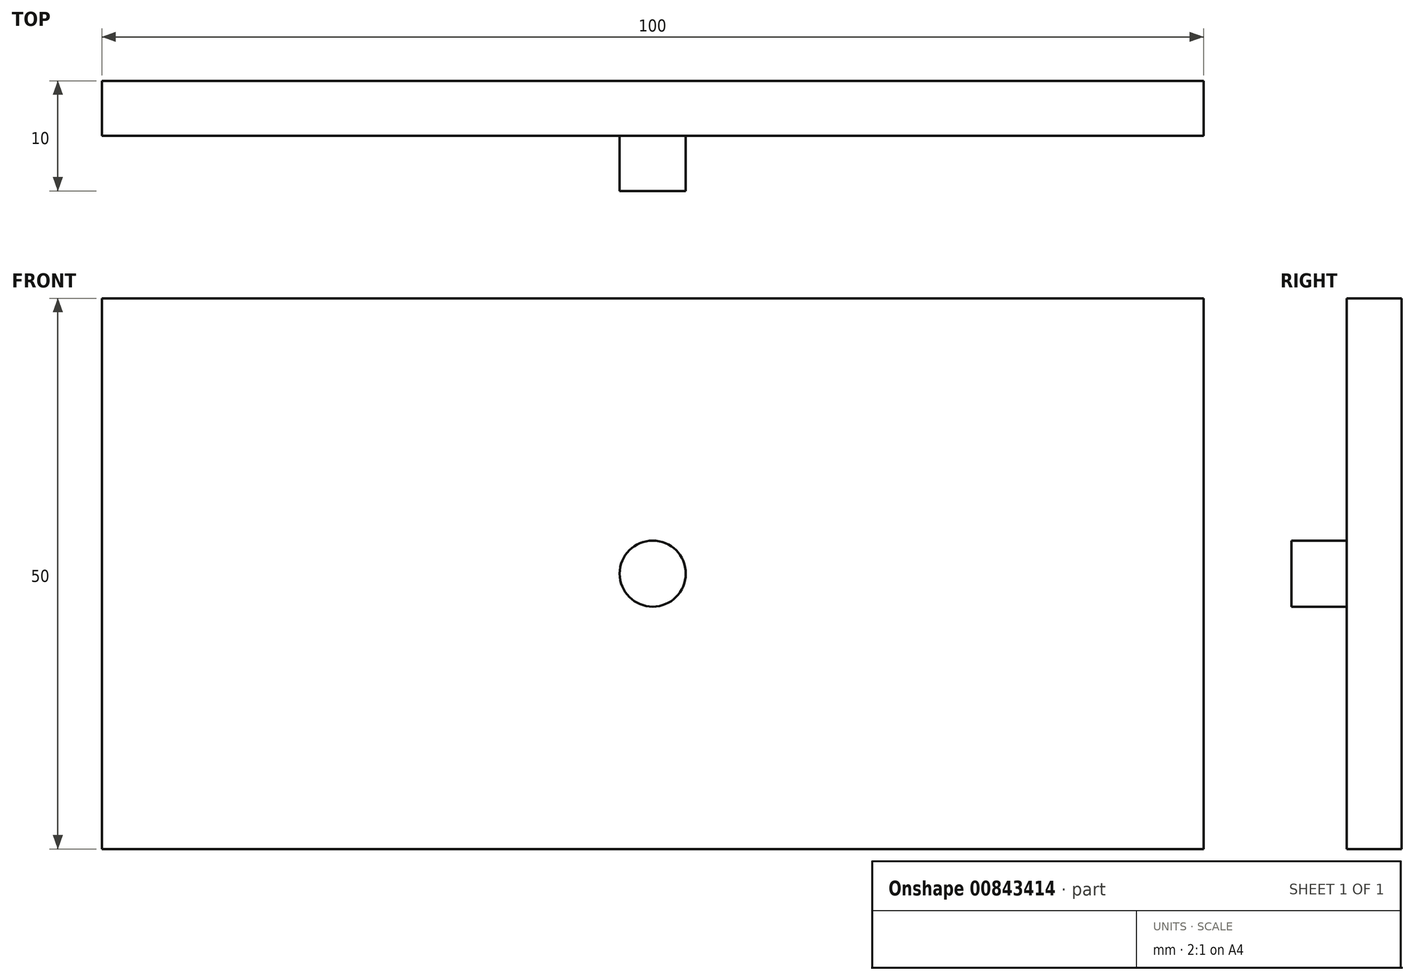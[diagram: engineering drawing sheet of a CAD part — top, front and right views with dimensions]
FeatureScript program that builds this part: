
annotation { "Feature Type Name" : "Feature", "Feature Type Description" : "" }
export const myFeature = defineFeature(function(context is Context, id is Id, definition is map)
    precondition{}
    {
        {
            var Q0;
            Q0=qCreatedBy(makeId("Front.planeOp"),FACE);
            var sketch = newSketch(context, id + "F0", { "sketchPlane" : qUnion([Q0])});
            skCircle(sketch, "E0", {"center": v(0, 0) * mm, "radius": 3 * mm});
            skLineSegment(sketch, "E1.bottom", {"start": v(-50, 25) * mm, "end": v(50, 25) * mm});
            skLineSegment(sketch, "E1.top", {"start": v(-50, -25) * mm, "end": v(50, -25) * mm});
            skLineSegment(sketch, "E1.left", {"start": v(-50, 25) * mm, "end": v(-50, -25) * mm});
            skLineSegment(sketch, "E1.right", {"start": v(50, 25) * mm, "end": v(50, -25) * mm});
            skSolve(sketch);
        }
        {
            var Q0;
            Q0=makeQuery(id+"F0.imprint","IMPRINT",FACE,{"disambiguationData":[TD([[makeQuery(id+"F0.imprint","IMPRINT",EDGE,{"derivedFrom":sQuery(id+"F0.wireOp",EDGE,"E0")}),-1.0]])]});
            var Q1;
            Q1=makeQuery(id+"F0.imprint","IMPRINT",FACE,{"disambiguationData":[TD([[makeQuery(id+"F0.imprint","IMPRINT",EDGE,{"derivedFrom":sQuery(id+"F0.wireOp",EDGE,"E0")}),1.0]])]});
            extrude(context, id + "F1", {"entities" : qUnion([Q0, Q1]), "depth" : 5 * mm, "offsetDistance" : 25 * mm});
        }
        {
            var Q0;
            Q0=makeQuery(id+"F0.imprint","IMPRINT",FACE,{"disambiguationData":[TD([[makeQuery(id+"F0.imprint","IMPRINT",EDGE,{"derivedFrom":sQuery(id+"F0.wireOp",EDGE,"E0")}),1.0]])]});
            extrude(context, id + "F2", {"entities" : qUnion([Q0]), "operationType" : NewBodyOperationType.ADD, "depth" : 10 * mm, "offsetDistance" : 25 * mm});
        }
    });
